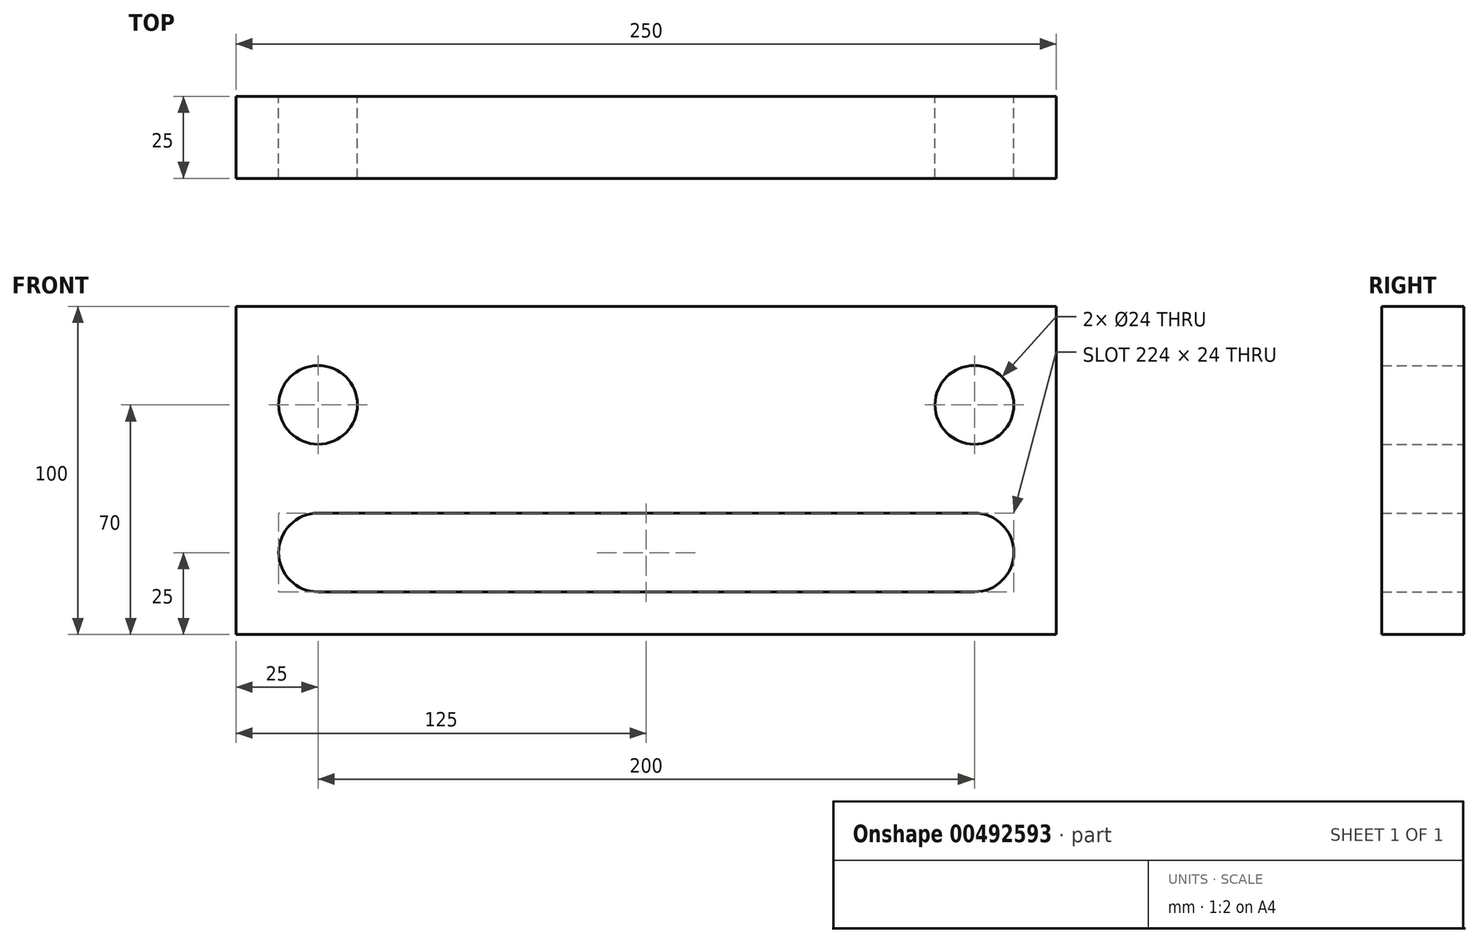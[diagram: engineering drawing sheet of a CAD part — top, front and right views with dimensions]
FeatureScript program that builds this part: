
annotation { "Feature Type Name" : "Feature", "Feature Type Description" : "" }
export const myFeature = defineFeature(function(context is Context, id is Id, definition is map)
    precondition{}
    {
        {
            var Q0;
            Q0=qCreatedBy(makeId("Front.planeOp"),FACE);
            var sketch = newSketch(context, id + "F0", { "sketchPlane" : qUnion([Q0])});
            skLineSegment(sketch, "E0.bottom", {"start": v(0, 0) * mm, "end": v(250, 0) * mm});
            skLineSegment(sketch, "E0.top", {"start": v(0, 100) * mm, "end": v(250, 100) * mm});
            skLineSegment(sketch, "E0.left", {"start": v(0, 0) * mm, "end": v(0, 100) * mm});
            skLineSegment(sketch, "E0.right", {"start": v(250, 0) * mm, "end": v(250, 100) * mm});
            skCircle(sketch, "E1", {"center": v(25, 70) * mm, "radius": 12 * mm});
            skArc(sketch, "E2", {"start": v(225, 13) * mm, "mid": v(237, 25) * mm, "end": v(225, 37) * mm});
            skCircle(sketch, "E3", {"center": v(225, 70) * mm, "radius": 12 * mm});
            skArc(sketch, "E4", {"start": v(25, 37) * mm, "mid": v(13, 25) * mm, "end": v(25, 13) * mm});
            skLineSegment(sketch, "E5", {"start": v(225, 37) * mm, "end": v(25, 37) * mm});
            skLineSegment(sketch, "E6", {"start": v(225, 13) * mm, "end": v(25, 13) * mm});
            skLineSegment(sketch, "E7", {"start": v(25, 70) * mm, "end": v(25, 25) * mm, "construction": true});
            skLineSegment(sketch, "E8", {"start": v(225, 70) * mm, "end": v(225, 25) * mm, "construction": true});
            skLineSegment(sketch, "E9", {"start": v(25, 70) * mm, "end": v(225, 70) * mm});
            skLineSegment(sketch, "E10", {"start": v(125, 100) * mm, "end": v(125, 0) * mm, "construction": true});
            skSolve(sketch);
        }
        {
            var Q0;
            Q0 = qSketchRegion(id + "F0", true);
            extrude(context, id + "F1", {"entities" : qUnion([Q0]), "depth" : 25 * mm});
        }
    });
